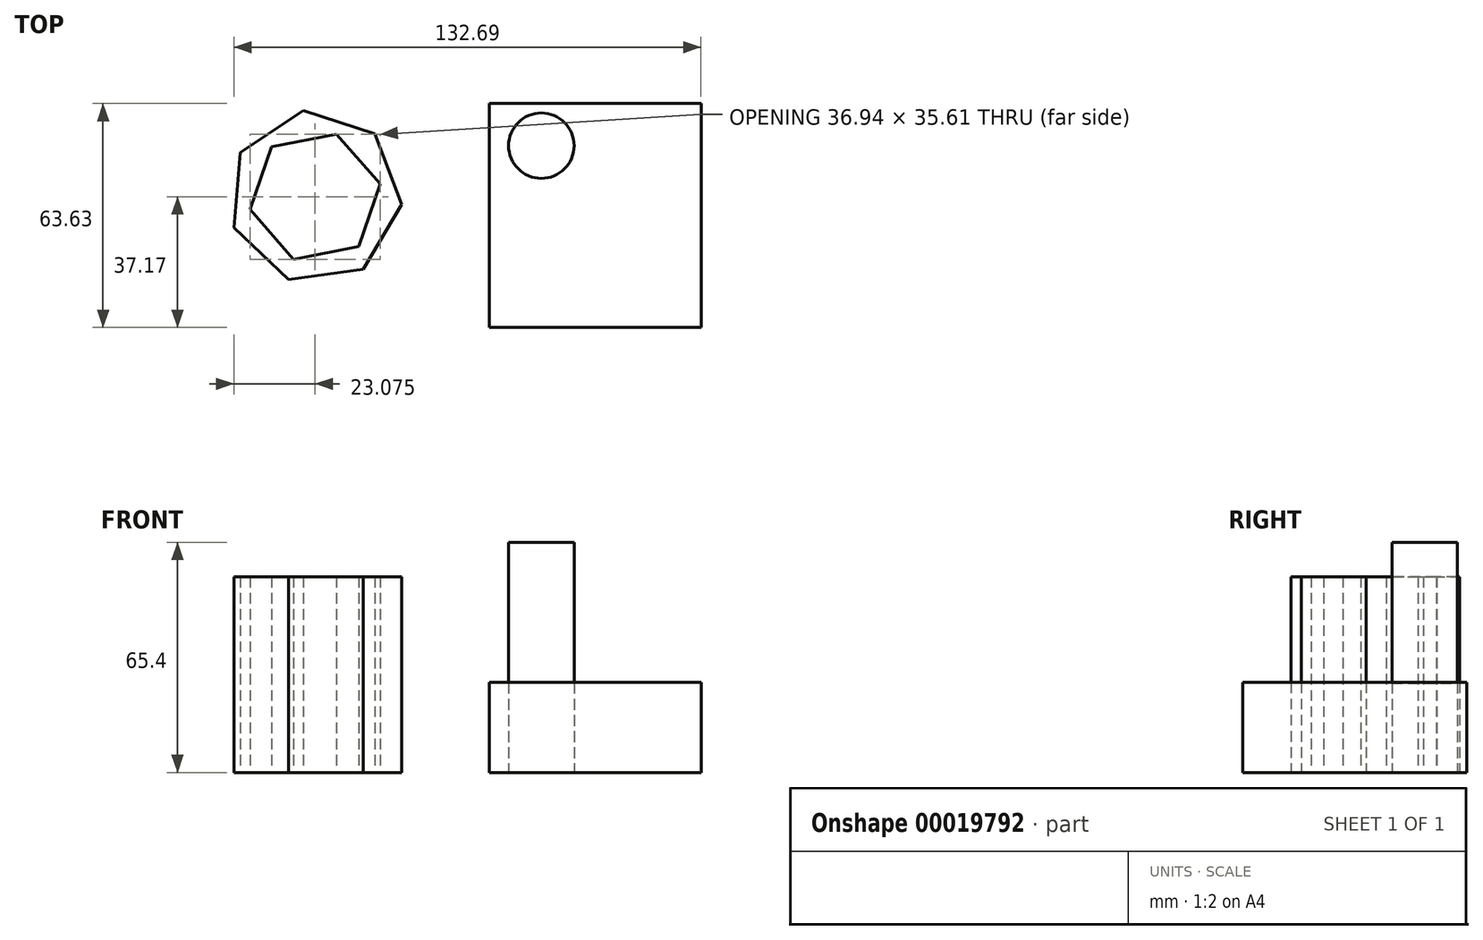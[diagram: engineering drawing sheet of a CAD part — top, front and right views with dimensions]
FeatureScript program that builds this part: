
annotation { "Feature Type Name" : "Feature", "Feature Type Description" : "" }
export const myFeature = defineFeature(function(context is Context, id is Id, definition is map)
    precondition{}
    {
        {
            var Q0;
            Q0=qCreatedBy(makeId("Top.planeOp"),FACE);
            var sketch = newSketch(context, id + "F0", { "sketchPlane" : qUnion([Q0])});
            skLineSegment(sketch, "E0.bottom", {"start": v(0, 0) * mm, "end": v(60.16, 0) * mm});
            skLineSegment(sketch, "E0.top", {"start": v(0, 63.63) * mm, "end": v(60.16, 63.63) * mm});
            skLineSegment(sketch, "E0.left", {"start": v(0, 0) * mm, "end": v(0, 63.63) * mm});
            skLineSegment(sketch, "E0.right", {"start": v(60.16, 0) * mm, "end": v(60.16, 63.63) * mm});
            skCircle(sketch, "E1.cCircle", {"center": v(-49.46, 37.17) * mm, "radius": 22.23 * mm, "construction": true});
            skLineSegment(sketch, "E1.0", {"start": v(-32.46, 55.06) * mm, "end": v(-24.87, 35.03) * mm});
            skLineSegment(sketch, "E1.1", {"start": v(-24.87, 35.03) * mm, "end": v(-35.8, 16.62) * mm});
            skLineSegment(sketch, "E1.2", {"start": v(-35.8, 16.62) * mm, "end": v(-57, 13.68) * mm});
            skLineSegment(sketch, "E1.3", {"start": v(-57, 13.68) * mm, "end": v(-72.53, 28.43) * mm});
            skLineSegment(sketch, "E1.4", {"start": v(-72.53, 28.43) * mm, "end": v(-70.68, 49.76) * mm});
            skLineSegment(sketch, "E1.5", {"start": v(-70.68, 49.76) * mm, "end": v(-52.84, 61.61) * mm});
            skLineSegment(sketch, "E1.6", {"start": v(-52.84, 61.61) * mm, "end": v(-32.46, 55.06) * mm});
            skPoint(sketch, "E1.0.midPoint", {"position": v(-28.67, 45.05) * mm});
            skCircle(sketch, "E2.cCircle", {"center": v(-49.46, 37.17) * mm, "radius": 16.3 * mm, "construction": true});
            skLineSegment(sketch, "E2.0", {"start": v(-43.35, 54.97) * mm, "end": v(-30.99, 40.79) * mm});
            skLineSegment(sketch, "E2.1", {"start": v(-30.99, 40.79) * mm, "end": v(-37.09, 22.98) * mm});
            skLineSegment(sketch, "E2.2", {"start": v(-37.09, 22.98) * mm, "end": v(-55.56, 19.37) * mm});
            skLineSegment(sketch, "E2.3", {"start": v(-55.56, 19.37) * mm, "end": v(-67.92, 33.55) * mm});
            skLineSegment(sketch, "E2.4", {"start": v(-67.92, 33.55) * mm, "end": v(-61.82, 51.36) * mm});
            skLineSegment(sketch, "E2.5", {"start": v(-61.82, 51.36) * mm, "end": v(-43.35, 54.97) * mm});
            skPoint(sketch, "E2.0.midPoint", {"position": v(-37.17, 47.88) * mm});
            skSolve(sketch);
        }
        {
            var Q0;
            Q0=makeQuery(id+"F0.imprint","IMPRINT",FACE,{"disambiguationData":[TD([[makeQuery(id+"F0.imprint","IMPRINT",EDGE,{"derivedFrom":sQuery(id+"F0.wireOp",EDGE,"E0.bottom")}),1.0]])]});
            extrude(context, id + "F1", {"entities" : qUnion([Q0]), "depth" : 25.58 * mm});
        }
        {
            var Q0;
            Q0=makeQuery(id+"F0.imprint","IMPRINT",FACE,{"disambiguationData":[TD([[makeQuery(id+"F0.imprint","IMPRINT",EDGE,{"derivedFrom":sQuery(id+"F0.wireOp",EDGE,"E1.0")}),-1.0]])]});
            extrude(context, id + "F2", {"entities" : qUnion([Q0]), "depth" : 55.6 * mm});
        }
        {
            var Q0;
            Q0=qCreatedBy(makeId("Top.planeOp"),FACE);
            var sketch = newSketch(context, id + "F3", { "sketchPlane" : qUnion([Q0])});
            skCircle(sketch, "E3", {"center": v(14.8, 51.66) * mm, "radius": 9.3 * mm});
            skSolve(sketch);
        }
        {
            var Q0;
            Q0 = qSketchRegion(id + "F3", true);
            extrude(context, id + "F4", {"entities" : qUnion([Q0]), "depth" : 25.4 * mm});
        }
        {
            var Q0;
            Q0=makeQuery(id+"F3.imprint","IMPRINT",FACE,{"disambiguationData":[TD([[makeQuery(id+"F3.imprint","IMPRINT",EDGE,{"derivedFrom":sQuery(id+"F3.wireOp",EDGE,"E3")}),1.0]])]});
            extrude(context, id + "F5", {"entities" : qUnion([Q0]), "depth" : 65.4 * mm});
        }
    });
